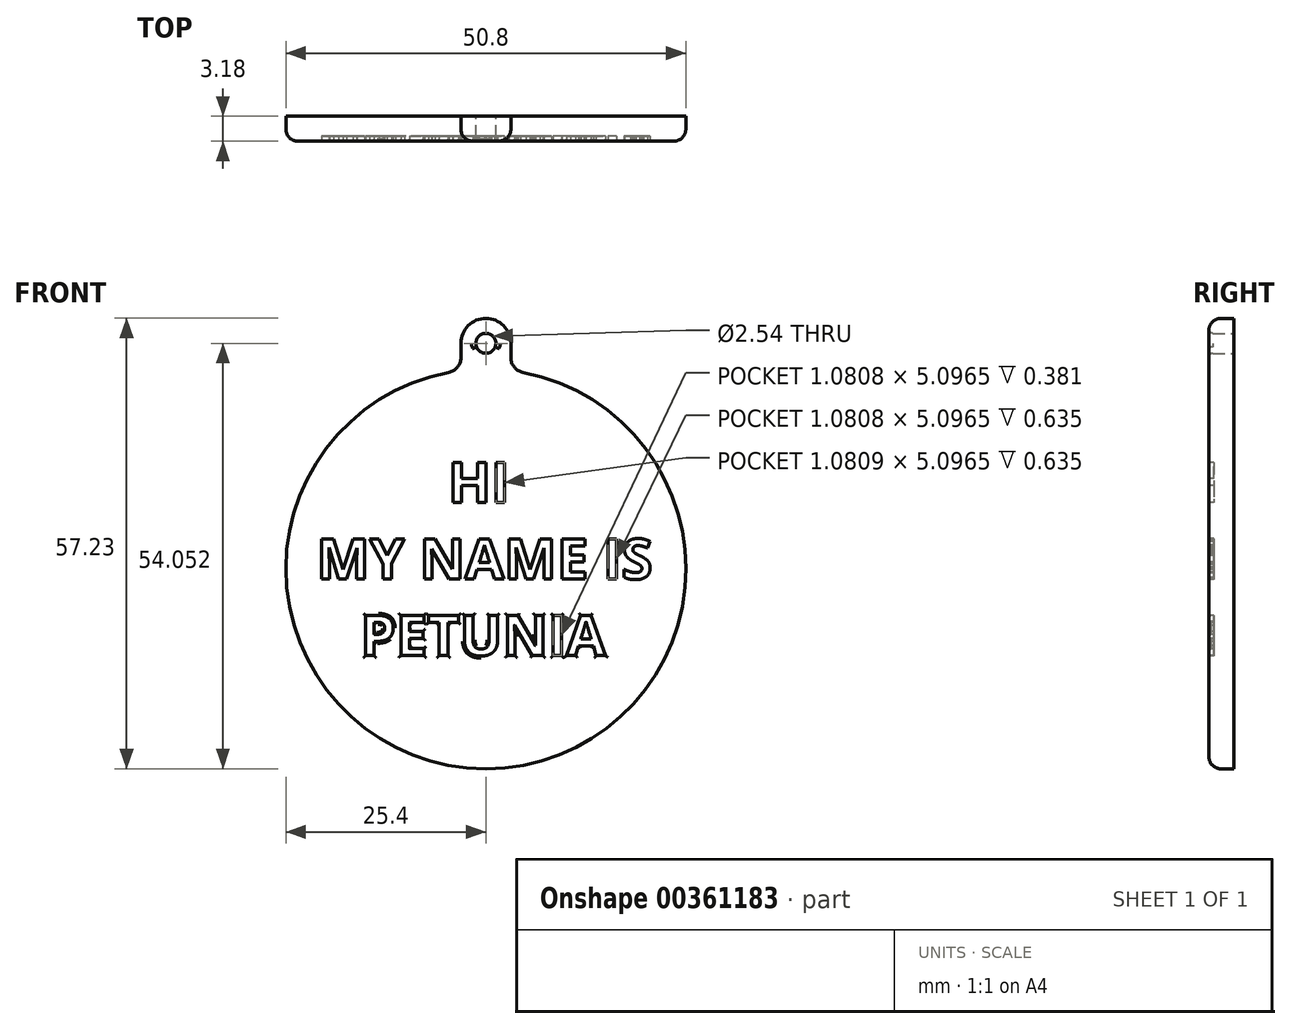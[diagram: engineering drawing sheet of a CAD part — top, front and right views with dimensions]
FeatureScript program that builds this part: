
annotation { "Feature Type Name" : "Feature", "Feature Type Description" : "" }
export const myFeature = defineFeature(function(context is Context, id is Id, definition is map)
    precondition{}
    {
        {
            var Q0;
            Q0=qCreatedBy(makeId("Front.planeOp"),FACE);
            var sketch = newSketch(context, id + "F0", { "sketchPlane" : qUnion([Q0])});
            skArc(sketch, "E0", {"start": v(-4.73, 24.96) * mm, "mid": v(0, -25.4) * mm, "end": v(4.73, 24.96) * mm});
            skCircle(sketch, "E1", {"center": v(0, 28.65) * mm, "radius": 1.27 * mm});
            skArc(sketch, "E2", {"start": v(3.18, 28.65) * mm, "mid": v(0, 31.83) * mm, "end": v(-3.18, 28.65) * mm});
            skLineSegment(sketch, "E3.left", {"start": v(-3.17, 26.83) * mm, "end": v(-3.17, 28.65) * mm});
            skLineSegment(sketch, "E3.right", {"start": v(3.18, 26.83) * mm, "end": v(3.18, 28.65) * mm});
            skPoint(sketch, "E3.top.end.orphan", {"position": v(3.18, 35) * mm});
            skPoint(sketch, "E3.top.start.orphan", {"position": v(-3.17, 35) * mm});
            skPoint(sketch, "E3.bottom.end.orphan", {"position": v(3.18, 22.3) * mm});
            skPoint(sketch, "E4.orphan", {"position": v(-3.17, 22.3) * mm});
            skPoint(sketch, "E5.visualSharp", {"position": v(-3.18, 25.2) * mm});
            skArc(sketch, "E5.filletArc", {"start": v(-4.73, 24.96) * mm, "mid": v(-3.61, 25.61) * mm, "end": v(-3.17, 26.83) * mm});
            skPoint(sketch, "E6.visualSharp", {"position": v(3.18, 25.2) * mm});
            skArc(sketch, "E6.filletArc", {"start": v(3.18, 26.83) * mm, "mid": v(3.61, 25.61) * mm, "end": v(4.73, 24.96) * mm});
            skSolve(sketch);
        }
        {
            var Q0;
            Q0 = qSketchRegion(id + "F0", true);
            extrude(context, id + "F1", {"entities" : qUnion([Q0]), "depth" : 3.17 * mm});
        }
        {
            var Q0;
            Q0=makeQuery(id+"F1.opExtrude","CAP_FACE",FACE,{"disambiguationData":[OSD([sQuery(id+"F0.wireOp",EDGE,"E0"),sQuery(id+"F0.wireOp",EDGE,"E1"),sQuery(id+"F0.wireOp",EDGE,"E2"),sQuery(id+"F0.wireOp",EDGE,"E3.left"),sQuery(id+"F0.wireOp",EDGE,"E3.right"),sQuery(id+"F0.wireOp",EDGE,"E5.filletArc"),sQuery(id+"F0.wireOp",EDGE,"E6.filletArc")])],"isStart":false});
            var sketch = newSketch(context, id + "F2", { "sketchPlane" : qUnion([Q0])});
            skText(sketch, "E7", { "text": "         HI\nMY NAME IS\n   PETUNIA", "fontName": "OpenSans-Bold.ttf"});
            const initialGuessF2  = {"E7": [-0.02149, 0.0084, 1, 0, 0.00514]};
            skSetInitialGuess(sketch, initialGuessF2);
            skSolve(sketch);
        }
        {
            var Q0;
            Q0 = qSketchRegion(id + "F2", true);
            extrude(context, id + "F3", {"entities" : qUnion([Q0]), "operationType" : NewBodyOperationType.REMOVE, "oppositeDirection" : true, "depth" : 0.64 * mm});
        }
        {
            var Q0;
            Q0=makeQuery(id+"F1.opExtrude","CAP_EDGE",EDGE,{"disambiguationData":[OSD([sQuery(id+"F0.wireOp",EDGE,"E0")])],"isStart":false});
            fillet(context, id + "F4", {"entities" : qUnion([Q0]), "radius" : 1.52 * mm, "tangentPropagation" : true, "allowEdgeOverflow" : false});
        }
        {
            var Q0;
            Q0=makeQuery(id+"F1.opExtrude","CAP_EDGE",EDGE,{"disambiguationData":[OSD([sQuery(id+"F0.wireOp",EDGE,"E1")])],"isStart":false});
            fillet(context, id + "F5", {"entities" : qUnion([Q0]), "radius" : 0.5 * mm, "tangentPropagation" : true, "allowEdgeOverflow" : false});
        }
        {
            var Q0;
            Q0=makeQuery(id+"F3.boolean.opBoolean","COPY",EDGE,{"derivedFrom":makeQuery(id+"F3.opExtrude","CAP_EDGE",EDGE,{"disambiguationData":[OSD([sQuery(id+"F2.wireOp",EDGE,"E7.sketch_text.stroke-145")])],"isStart":true})});
            var Q1;
            Q1=makeQuery(id+"F3.boolean.opBoolean","COPY",EDGE,{"derivedFrom":makeQuery(id+"F3.opExtrude","CAP_EDGE",EDGE,{"disambiguationData":[OSD([sQuery(id+"F2.wireOp",EDGE,"E7.sketch_text.stroke-144")])],"isStart":true})});
            var Q2;
            Q2=makeQuery(id+"F3.boolean.opBoolean","COPY",EDGE,{"derivedFrom":makeQuery(id+"F3.opExtrude","CAP_EDGE",EDGE,{"disambiguationData":[OSD([sQuery(id+"F2.wireOp",EDGE,"E7.sketch_text.stroke-143")])],"isStart":true})});
            var Q3;
            Q3=makeQuery(id+"F3.boolean.opBoolean","COPY",EDGE,{"derivedFrom":makeQuery(id+"F3.opExtrude","CAP_EDGE",EDGE,{"disambiguationData":[OSD([sQuery(id+"F2.wireOp",EDGE,"E7.sketch_text.stroke-141")])],"isStart":true})});
            var Q4;
            Q4=makeQuery(id+"F3.boolean.opBoolean","COPY",EDGE,{"derivedFrom":makeQuery(id+"F3.opExtrude","CAP_EDGE",EDGE,{"disambiguationData":[OSD([sQuery(id+"F2.wireOp",EDGE,"E7.sketch_text.stroke-134")])],"isStart":true})});
            var Q5;
            Q5=makeQuery(id+"F3.boolean.opBoolean","COPY",EDGE,{"derivedFrom":makeQuery(id+"F3.opExtrude","CAP_EDGE",EDGE,{"disambiguationData":[OSD([sQuery(id+"F2.wireOp",EDGE,"E7.sketch_text.stroke-139")])],"isStart":true})});
            var Q6;
            Q6=makeQuery(id+"F3.boolean.opBoolean","COPY",EDGE,{"derivedFrom":makeQuery(id+"F3.opExtrude","CAP_EDGE",EDGE,{"disambiguationData":[OSD([sQuery(id+"F2.wireOp",EDGE,"E7.sketch_text.stroke-150")])],"isStart":true})});
            var Q7;
            Q7=makeQuery(id+"F3.boolean.opBoolean","COPY",EDGE,{"derivedFrom":makeQuery(id+"F3.opExtrude","CAP_EDGE",EDGE,{"disambiguationData":[OSD([sQuery(id+"F2.wireOp",EDGE,"E7.sketch_text.stroke-151")])],"isStart":true})});
            var Q8;
            Q8=makeQuery(id+"F3.boolean.opBoolean","COPY",EDGE,{"derivedFrom":makeQuery(id+"F3.opExtrude","CAP_EDGE",EDGE,{"disambiguationData":[OSD([sQuery(id+"F2.wireOp",EDGE,"E7.sketch_text.stroke-149")])],"isStart":true})});
            var Q9;
            Q9=makeQuery(id+"F3.boolean.opBoolean","COPY",EDGE,{"derivedFrom":makeQuery(id+"F3.opExtrude","CAP_EDGE",EDGE,{"disambiguationData":[OSD([sQuery(id+"F2.wireOp",EDGE,"E7.sketch_text.stroke-159")])],"isStart":true})});
            var Q10;
            Q10=makeQuery(id+"F3.boolean.opBoolean","COPY",EDGE,{"derivedFrom":makeQuery(id+"F3.opExtrude","CAP_EDGE",EDGE,{"disambiguationData":[OSD([sQuery(id+"F2.wireOp",EDGE,"E7.sketch_text.stroke-157")])],"isStart":true})});
            var Q11;
            Q11=makeQuery(id+"F3.boolean.opBoolean","COPY",EDGE,{"derivedFrom":makeQuery(id+"F3.opExtrude","CAP_EDGE",EDGE,{"disambiguationData":[OSD([sQuery(id+"F2.wireOp",EDGE,"E7.sketch_text.stroke-155")])],"isStart":true})});
            var Q12;
            Q12=makeQuery(id+"F3.boolean.opBoolean","COPY",EDGE,{"derivedFrom":makeQuery(id+"F3.opExtrude","CAP_EDGE",EDGE,{"disambiguationData":[OSD([sQuery(id+"F2.wireOp",EDGE,"E7.sketch_text.stroke-153")])],"isStart":true})});
            var Q13;
            Q13=makeQuery(id+"F3.boolean.opBoolean","COPY",EDGE,{"derivedFrom":makeQuery(id+"F3.opExtrude","CAP_EDGE",EDGE,{"disambiguationData":[OSD([sQuery(id+"F2.wireOp",EDGE,"E7.sketch_text.stroke-152")])],"isStart":true})});
            var Q14;
            Q14=makeQuery(id+"F3.boolean.opBoolean","COPY",EDGE,{"derivedFrom":makeQuery(id+"F3.opExtrude","CAP_EDGE",EDGE,{"disambiguationData":[OSD([sQuery(id+"F2.wireOp",EDGE,"E7.sketch_text.stroke-156")])],"isStart":true})});
            var Q15;
            Q15=makeQuery(id+"F3.boolean.opBoolean","COPY",EDGE,{"derivedFrom":makeQuery(id+"F3.opExtrude","CAP_EDGE",EDGE,{"disambiguationData":[OSD([sQuery(id+"F2.wireOp",EDGE,"E7.sketch_text.stroke-160")])],"isStart":true})});
            var Q16;
            Q16=makeQuery(id+"F3.boolean.opBoolean","COPY",EDGE,{"derivedFrom":makeQuery(id+"F3.opExtrude","CAP_EDGE",EDGE,{"disambiguationData":[OSD([sQuery(id+"F2.wireOp",EDGE,"E7.sketch_text.stroke-158")])],"isStart":true})});
            var Q17;
            Q17=makeQuery(id+"F3.boolean.opBoolean","COPY",EDGE,{"derivedFrom":makeQuery(id+"F3.opExtrude","CAP_EDGE",EDGE,{"disambiguationData":[OSD([sQuery(id+"F2.wireOp",EDGE,"E7.sketch_text.stroke-154")])],"isStart":true})});
            fillet(context, id + "F6", {"entities" : qUnion([Q0, Q1, Q2, Q3, Q4, Q5, Q6, Q7, Q8, Q9, Q10, Q11, Q12, Q13, Q14, Q15, Q16, Q17]), "radius" : 0.25 * mm, "tangentPropagation" : true, "allowEdgeOverflow" : false});
        }
        {
            var Q0;
            Q0=makeQuery(id+"F3.boolean.opBoolean","COPY",EDGE,{"derivedFrom":makeQuery(id+"F3.opExtrude","CAP_EDGE",EDGE,{"disambiguationData":[OSD([sQuery(id+"F2.wireOp",EDGE,"E7.sketch_text.stroke-162")])],"isStart":true})});
            var Q1;
            Q1=makeQuery(id+"F3.boolean.opBoolean","COPY",EDGE,{"derivedFrom":makeQuery(id+"F3.opExtrude","CAP_EDGE",EDGE,{"disambiguationData":[OSD([sQuery(id+"F2.wireOp",EDGE,"E7.sketch_text.stroke-168")])],"isStart":true})});
            var Q2;
            Q2=makeQuery(id+"F3.boolean.opBoolean","COPY",EDGE,{"derivedFrom":makeQuery(id+"F3.opExtrude","CAP_EDGE",EDGE,{"disambiguationData":[OSD([sQuery(id+"F2.wireOp",EDGE,"E7.sketch_text.stroke-161")])],"isStart":true})});
            var Q3;
            Q3=makeQuery(id+"F3.boolean.opBoolean","COPY",EDGE,{"derivedFrom":makeQuery(id+"F3.opExtrude","CAP_EDGE",EDGE,{"disambiguationData":[OSD([sQuery(id+"F2.wireOp",EDGE,"E7.sketch_text.stroke-165")])],"isStart":true})});
            var Q4;
            Q4=makeQuery(id+"F3.boolean.opBoolean","COPY",EDGE,{"derivedFrom":makeQuery(id+"F3.opExtrude","CAP_EDGE",EDGE,{"disambiguationData":[OSD([sQuery(id+"F2.wireOp",EDGE,"E7.sketch_text.stroke-167")])],"isStart":true})});
            var Q5;
            Q5=makeQuery(id+"F3.boolean.opBoolean","COPY",EDGE,{"derivedFrom":makeQuery(id+"F3.opExtrude","CAP_EDGE",EDGE,{"disambiguationData":[OSD([sQuery(id+"F2.wireOp",EDGE,"E7.sketch_text.stroke-163")])],"isStart":true})});
            var Q6;
            Q6=makeQuery(id+"F3.boolean.opBoolean","COPY",EDGE,{"derivedFrom":makeQuery(id+"F3.opExtrude","CAP_EDGE",EDGE,{"disambiguationData":[OSD([sQuery(id+"F2.wireOp",EDGE,"E7.sketch_text.stroke-164")])],"isStart":true})});
            var Q7;
            Q7=makeQuery(id+"F3.boolean.opBoolean","COPY",EDGE,{"derivedFrom":makeQuery(id+"F3.opExtrude","CAP_EDGE",EDGE,{"disambiguationData":[OSD([sQuery(id+"F2.wireOp",EDGE,"E7.sketch_text.stroke-166")])],"isStart":true})});
            var Q8;
            Q8=makeQuery(id+"F3.boolean.opBoolean","COPY",EDGE,{"derivedFrom":makeQuery(id+"F3.opExtrude","CAP_EDGE",EDGE,{"disambiguationData":[OSD([sQuery(id+"F2.wireOp",EDGE,"E7.sketch_text.stroke-175")])],"isStart":true})});
            var Q9;
            Q9=makeQuery(id+"F3.boolean.opBoolean","COPY",EDGE,{"derivedFrom":makeQuery(id+"F3.opExtrude","CAP_EDGE",EDGE,{"disambiguationData":[OSD([sQuery(id+"F2.wireOp",EDGE,"E7.sketch_text.stroke-176")])],"isStart":true})});
            var Q10;
            Q10=makeQuery(id+"F3.boolean.opBoolean","COPY",EDGE,{"derivedFrom":makeQuery(id+"F3.opExtrude","CAP_EDGE",EDGE,{"disambiguationData":[OSD([sQuery(id+"F2.wireOp",EDGE,"E7.sketch_text.stroke-177")])],"isStart":true})});
            var Q11;
            Q11=makeQuery(id+"F3.boolean.opBoolean","COPY",EDGE,{"derivedFrom":makeQuery(id+"F3.opExtrude","CAP_EDGE",EDGE,{"disambiguationData":[OSD([sQuery(id+"F2.wireOp",EDGE,"E7.sketch_text.stroke-183")])],"isStart":true})});
            fillet(context, id + "F7", {"entities" : qUnion([Q0, Q1, Q2, Q3, Q4, Q5, Q6, Q7, Q8, Q9, Q10, Q11]), "radius" : 0.25 * mm, "tangentPropagation" : true, "allowEdgeOverflow" : false});
        }
        {
            var Q0;
            Q0=makeQuery(id+"F3.boolean.opBoolean","COPY",EDGE,{"derivedFrom":makeQuery(id+"F3.opExtrude","CAP_EDGE",EDGE,{"disambiguationData":[OSD([sQuery(id+"F2.wireOp",EDGE,"E7.sketch_text.stroke-190")])],"isStart":true})});
            var Q1;
            Q1=makeQuery(id+"F3.boolean.opBoolean","COPY",EDGE,{"derivedFrom":makeQuery(id+"F3.opExtrude","CAP_EDGE",EDGE,{"disambiguationData":[OSD([sQuery(id+"F2.wireOp",EDGE,"E7.sketch_text.stroke-191")])],"isStart":true})});
            var Q2;
            Q2=makeQuery(id+"F3.boolean.opBoolean","COPY",EDGE,{"derivedFrom":makeQuery(id+"F3.opExtrude","CAP_EDGE",EDGE,{"disambiguationData":[OSD([sQuery(id+"F2.wireOp",EDGE,"E7.sketch_text.stroke-192")])],"isStart":true})});
            var Q3;
            Q3=makeQuery(id+"F3.boolean.opBoolean","COPY",EDGE,{"derivedFrom":makeQuery(id+"F3.opExtrude","CAP_EDGE",EDGE,{"disambiguationData":[OSD([sQuery(id+"F2.wireOp",EDGE,"E7.sketch_text.stroke-195")])],"isStart":true})});
            var Q4;
            Q4=makeQuery(id+"F3.boolean.opBoolean","COPY",EDGE,{"derivedFrom":makeQuery(id+"F3.opExtrude","CAP_EDGE",EDGE,{"disambiguationData":[OSD([sQuery(id+"F2.wireOp",EDGE,"E7.sketch_text.stroke-196")])],"isStart":true})});
            var Q5;
            Q5=makeQuery(id+"F3.boolean.opBoolean","COPY",EDGE,{"derivedFrom":makeQuery(id+"F3.opExtrude","CAP_EDGE",EDGE,{"disambiguationData":[OSD([sQuery(id+"F2.wireOp",EDGE,"E7.sketch_text.stroke-197")])],"isStart":true})});
            var Q6;
            Q6=makeQuery(id+"F3.boolean.opBoolean","COPY",EDGE,{"derivedFrom":makeQuery(id+"F3.opExtrude","CAP_EDGE",EDGE,{"disambiguationData":[OSD([sQuery(id+"F2.wireOp",EDGE,"E7.sketch_text.stroke-184")])],"isStart":true})});
            var Q7;
            Q7=makeQuery(id+"F3.boolean.opBoolean","COPY",EDGE,{"derivedFrom":makeQuery(id+"F3.opExtrude","CAP_EDGE",EDGE,{"disambiguationData":[OSD([sQuery(id+"F2.wireOp",EDGE,"E7.sketch_text.stroke-185")])],"isStart":true})});
            var Q8;
            Q8=makeQuery(id+"F3.boolean.opBoolean","COPY",EDGE,{"derivedFrom":makeQuery(id+"F3.opExtrude","CAP_EDGE",EDGE,{"disambiguationData":[OSD([sQuery(id+"F2.wireOp",EDGE,"E7.sketch_text.stroke-188")])],"isStart":true})});
            var Q9;
            Q9=makeQuery(id+"F3.boolean.opBoolean","COPY",EDGE,{"derivedFrom":makeQuery(id+"F3.opExtrude","CAP_EDGE",EDGE,{"disambiguationData":[OSD([sQuery(id+"F2.wireOp",EDGE,"E7.sketch_text.stroke-189")])],"isStart":true})});
            var Q10;
            Q10=makeQuery(id+"F3.boolean.opBoolean","COPY",EDGE,{"derivedFrom":makeQuery(id+"F3.opExtrude","CAP_EDGE",EDGE,{"disambiguationData":[OSD([sQuery(id+"F2.wireOp",EDGE,"E7.sketch_text.stroke-198")])],"isStart":true})});
            var Q11;
            Q11=makeQuery(id+"F3.boolean.opBoolean","COPY",EDGE,{"derivedFrom":makeQuery(id+"F3.opExtrude","CAP_EDGE",EDGE,{"disambiguationData":[OSD([sQuery(id+"F2.wireOp",EDGE,"E7.sketch_text.stroke-199")])],"isStart":true})});
            var Q12;
            Q12=makeQuery(id+"F3.boolean.opBoolean","COPY",EDGE,{"derivedFrom":makeQuery(id+"F3.opExtrude","CAP_EDGE",EDGE,{"disambiguationData":[OSD([sQuery(id+"F2.wireOp",EDGE,"E7.sketch_text.stroke-200")])],"isStart":true})});
            var Q13;
            Q13=makeQuery(id+"F3.boolean.opBoolean","COPY",EDGE,{"derivedFrom":makeQuery(id+"F3.opExtrude","CAP_EDGE",EDGE,{"disambiguationData":[OSD([sQuery(id+"F2.wireOp",EDGE,"E7.sketch_text.stroke-201")])],"isStart":true})});
            var Q14;
            Q14=makeQuery(id+"F3.boolean.opBoolean","COPY",EDGE,{"derivedFrom":makeQuery(id+"F3.opExtrude","CAP_EDGE",EDGE,{"disambiguationData":[OSD([sQuery(id+"F2.wireOp",EDGE,"E7.sketch_text.stroke-206")])],"isStart":true})});
            var Q15;
            Q15=makeQuery(id+"F3.boolean.opBoolean","COPY",EDGE,{"derivedFrom":makeQuery(id+"F3.opExtrude","CAP_EDGE",EDGE,{"disambiguationData":[OSD([sQuery(id+"F2.wireOp",EDGE,"E7.sketch_text.stroke-207")])],"isStart":true})});
            var Q16;
            Q16=makeQuery(id+"F3.boolean.opBoolean","COPY",EDGE,{"derivedFrom":makeQuery(id+"F3.opExtrude","CAP_EDGE",EDGE,{"disambiguationData":[OSD([sQuery(id+"F2.wireOp",EDGE,"E7.sketch_text.stroke-208")])],"isStart":true})});
            var Q17;
            Q17=makeQuery(id+"F3.boolean.opBoolean","COPY",EDGE,{"derivedFrom":makeQuery(id+"F3.opExtrude","CAP_EDGE",EDGE,{"disambiguationData":[OSD([sQuery(id+"F2.wireOp",EDGE,"E7.sketch_text.stroke-209")])],"isStart":true})});
            var Q18;
            Q18=makeQuery(id+"F3.boolean.opBoolean","COPY",EDGE,{"derivedFrom":makeQuery(id+"F3.opExtrude","CAP_EDGE",EDGE,{"disambiguationData":[OSD([sQuery(id+"F2.wireOp",EDGE,"E7.sketch_text.stroke-203")])],"isStart":true})});
            var Q19;
            Q19=makeQuery(id+"F3.boolean.opBoolean","COPY",EDGE,{"derivedFrom":makeQuery(id+"F3.opExtrude","CAP_EDGE",EDGE,{"disambiguationData":[OSD([sQuery(id+"F2.wireOp",EDGE,"E7.sketch_text.stroke-205")])],"isStart":true})});
            var Q20;
            Q20=makeQuery(id+"F3.boolean.opBoolean","COPY",EDGE,{"derivedFrom":makeQuery(id+"F3.opExtrude","CAP_EDGE",EDGE,{"disambiguationData":[OSD([sQuery(id+"F2.wireOp",EDGE,"E7.sketch_text.stroke-204")])],"isStart":true})});
            var Q21;
            Q21=makeQuery(id+"F3.boolean.opBoolean","COPY",EDGE,{"derivedFrom":makeQuery(id+"F3.opExtrude","CAP_EDGE",EDGE,{"disambiguationData":[OSD([sQuery(id+"F2.wireOp",EDGE,"E7.sketch_text.stroke-202")])],"isStart":true})});
            var Q22;
            Q22=makeQuery(id+"F3.boolean.opBoolean","COPY",EDGE,{"derivedFrom":makeQuery(id+"F3.opExtrude","CAP_EDGE",EDGE,{"disambiguationData":[OSD([sQuery(id+"F2.wireOp",EDGE,"E7.sketch_text.stroke-213")])],"isStart":true})});
            var Q23;
            Q23=makeQuery(id+"F3.boolean.opBoolean","COPY",EDGE,{"derivedFrom":makeQuery(id+"F3.opExtrude","CAP_EDGE",EDGE,{"disambiguationData":[OSD([sQuery(id+"F2.wireOp",EDGE,"E7.sketch_text.stroke-212")])],"isStart":true})});
            var Q24;
            Q24=makeQuery(id+"F3.boolean.opBoolean","COPY",EDGE,{"derivedFrom":makeQuery(id+"F3.opExtrude","CAP_EDGE",EDGE,{"disambiguationData":[OSD([sQuery(id+"F2.wireOp",EDGE,"E7.sketch_text.stroke-210")])],"isStart":true})});
            fillet(context, id + "F8", {"entities" : qUnion([Q0, Q1, Q2, Q3, Q4, Q5, Q6, Q7, Q8, Q9, Q10, Q11, Q12, Q13, Q14, Q15, Q16, Q17, Q18, Q19, Q20, Q21, Q22, Q23, Q24]), "radius" : 0.25 * mm, "tangentPropagation" : true, "allowEdgeOverflow" : false});
        }
    });
